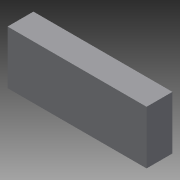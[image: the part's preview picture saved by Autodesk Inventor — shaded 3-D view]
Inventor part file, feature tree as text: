
AUTODESK INVENTOR PART (.ipt)
format: ipt  version: 2013 (Build 170138000, 138)  size: 67,072 bytes
history: native  units: mm
features: extrude x1, sketch x1
ambient origin geometry x8: Origin, YZ Plane, XZ Plane, XY Plane, X Axis, Y Axis, Z Axis, Center Point
bodies: Solid1 (feature_tree)
feature tree (2):
  extrude  "Extrusion1"  Depth=16.5mm
  sketch  "Sketch1"  dims[d0=43.0mm d1=16.5mm d2=8.0mm d3=0.0mm]
